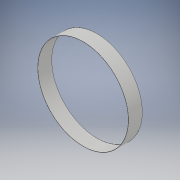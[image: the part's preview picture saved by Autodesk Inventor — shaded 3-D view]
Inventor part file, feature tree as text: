
AUTODESK INVENTOR PART (.ipt)
format: ipt  version: 2019 (Build 230136000, 136)  size: 104,448 bytes
history: native  units: mm
features: extrude x2, sketch x2
ambient origin geometry x8: Origin, YZ Plane, XZ Plane, XY Plane, X Axis, Y Axis, Z Axis, Center Point
bodies: Solid1 (feature_tree)
feature tree (4):
  extrude  "Extrusion1"  Depth=9.555mm TaperAngle=0.0deg
  extrude  "Extrusion2"  Depth=9.555mm TaperAngle=0.0deg
  sketch  "Sketch1"  dims[d0=62.9mm d1=9.555mm d2=0.0mm]
  sketch  "Sketch2"  dims[d3=62.6mm d4=9.555mm d5=0.0mm]
